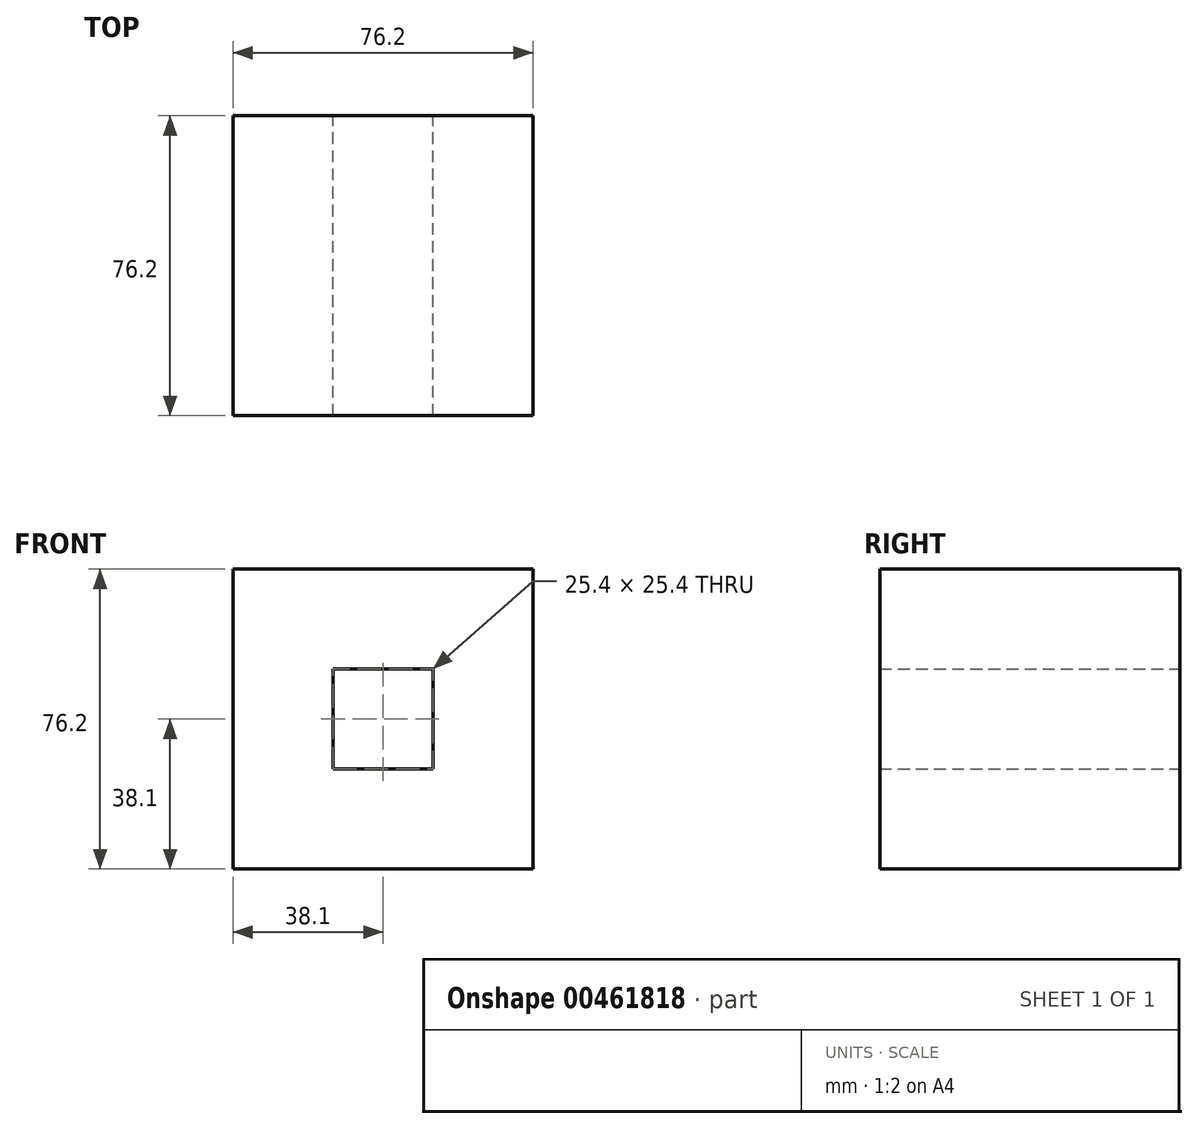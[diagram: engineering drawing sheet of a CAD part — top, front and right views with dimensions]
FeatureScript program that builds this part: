
annotation { "Feature Type Name" : "Feature", "Feature Type Description" : "" }
export const myFeature = defineFeature(function(context is Context, id is Id, definition is map)
    precondition{}
    {
        {
            var Q0;
            Q0=qCreatedBy(makeId("Front.planeOp"),FACE);
            var sketch = newSketch(context, id + "F0", { "sketchPlane" : qUnion([Q0])});
            skLineSegment(sketch, "E0.bottom", {"start": v(-38.1, 38.1) * mm, "end": v(38.1, 38.1) * mm});
            skLineSegment(sketch, "E0.top", {"start": v(-38.1, -38.1) * mm, "end": v(38.1, -38.1) * mm});
            skLineSegment(sketch, "E0.left", {"start": v(-38.1, 38.1) * mm, "end": v(-38.1, -38.1) * mm});
            skLineSegment(sketch, "E0.right", {"start": v(38.1, 38.1) * mm, "end": v(38.1, -38.1) * mm});
            skPoint(sketch, "E0.middle", {"position": v(0, 0) * mm});
            skSolve(sketch);
        }
        {
            var Q0;
            Q0=makeQuery(id+"F0.imprint","IMPRINT",FACE,{"disambiguationData":[TD([[makeQuery(id+"F0.imprint","IMPRINT",EDGE,{"derivedFrom":sQuery(id+"F0.wireOp",EDGE,"E0.bottom")}),-1.0]])]});
            var sketch = newSketch(context, id + "F1", { "sketchPlane" : qUnion([Q0])});
            skLineSegment(sketch, "E1.bottom", {"start": v(12.7, 12.7) * mm, "end": v(-12.7, 12.7) * mm});
            skLineSegment(sketch, "E1.top", {"start": v(12.7, -12.7) * mm, "end": v(-12.7, -12.7) * mm});
            skLineSegment(sketch, "E1.left", {"start": v(12.7, 12.7) * mm, "end": v(12.7, -12.7) * mm});
            skLineSegment(sketch, "E1.right", {"start": v(-12.7, 12.7) * mm, "end": v(-12.7, -12.7) * mm});
            skPoint(sketch, "E1.middle", {"position": v(0, 0) * mm});
            skSolve(sketch);
        }
        {
            var Q0;
            Q0 = qSketchRegion(id + "F0", true);
            extrude(context, id + "F2", {"entities" : qUnion([Q0]), "depth" : 76.2 * mm, "offsetDistance" : 25.4 * mm});
        }
        {
            var Q0;
            Q0 = qSketchRegion(id + "F1", true);
            extrude(context, id + "F3", {"entities" : qUnion([Q0]), "operationType" : NewBodyOperationType.REMOVE, "endBound" : BoundingType.THROUGH_ALL, "depth" : 76.2 * mm});
        }
    });
